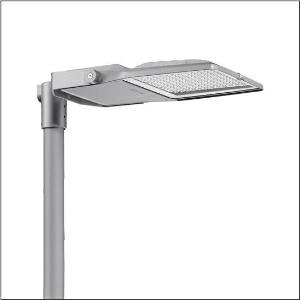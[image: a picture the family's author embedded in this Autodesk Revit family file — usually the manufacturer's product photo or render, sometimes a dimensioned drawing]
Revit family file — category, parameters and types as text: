
# Revit family: floodlight_fl_21_iq_midi___pl61_5xa7781e2c3a_352e
name_source: partatom
category: Lighting Fixtures
units: mm (PartAtom-declared; Revit-internal decimal feet)

## family parameters
Cut with Voids When Loaded = No
Host = Face
Light Source = No
Part Type = Normal
Room Calculation Point = No
Round Connector Dimension = Use Diameter
Shared = No

## types (1)
- --- (1 x LED, 26360 lm, 208.1 W, 3000K)
    Apparent Load = 208 VA
    CIE Flux Codes = 33 65 98 100 100
    Color Rendering = 70
    Color Temperature = 3000K
    Default Elevation = 1800 mm
    Description = Floodlight FL 21 iQ midi, floodlight, primary light control with lens, of PMMA, primary optical cover: protective disc, of toughened safety glass, transparent, light distribution: PL61, light emission: direct distribution, installation type: surface-mounted, LED, High Power LED, rated luminous flux: 26.360lm, luminous efficacy: 127lm/W, light colour: 730, colour temperature: 3000K, control gear: ECG iQ, control: optimised constant luminous flux control (CLO 2.0), Desk-Remote (wireless, voltage-free reading and setting of iQ features in the workshop via application-optimized NFC function/RFID function), Light-Fading, Smart-Wire, Night-Set, Lumen-Switch, Temp-Guard, Auto-Match, with terminal, 6-pole, mains connection: 220..240V, AC, 50/60Hz, start of lifetime: 208W, end of service life: 227W, reduction: 90W, luminaire housing, of diecast aluminium, powder-coated, Siteco® metallic grey (DB 702S), corrosivity category C5 mid according to DIN EN ISO 12944, sealing non-destructively replaceable, please order mast flange separately, mast bracket, of steel, galvanised, powder-coated, Siteco® metallic grey (DB 702S), protection rating (complete): IP66, insulation class (complete): insulation class II (safety insulation), certification: CE, protection symbol: D, impact resistance: IK08, permissible operating ambient temperature: -40..+40°C, permissible operating ambient temperature for outdoor applications: -40..+50°C, standard: DIN EN 12944, LABS conformity tested according to VDMA 24364:2018-05, packaging unit: 1 piece

Light Distribution: PL61
    Height = 76 mm
    Lamp = 1 x LED
    Lamp Light Flux = 26360 lm
    Lamp Power = 208.1 W
    Lamp count = 1
    Length = 657 mm
    Luminous efficacy = 127 lm/W
    Manufacturer = Siteco
    ModVariant = No
    Model = 5XA7781E2C3A
    Number of Poles = 1
    OnlyDefault = Yes
    Power Factor = 1
    Product Name = Floodlight FL 21 iQ midi | PL61
    Product group = floodlight | pylon annexe
    ProductGroupID = 6200
    Protection Class = Protection class II
    Protection Degree = IP 66
    RLX_Detail_Level = 1
    RLX_Emergency_Light_Flux = 0 lm
    RLX_Emergency_Type = 0
    RLX_Emergency_Type_DB = No
    RlxData = <blob elided: 153649 chars, md5=3d2aee96>
    Socket = socket
    Standby Power = 0 W
    System Light Flux = 26360 lm
    System Power = 208 W
    Type Comments = factory setting: luminous flux: 100 % | dim-lin: 254 | 710 mA
    Type Image = l_1007123.jpg
    URL = http://relux.com
    VarID = @adj_057223
    Voltage = 0 V
    Weight = 0.00 kg
    Width = 442 mm

## geometry (parser evidence)
native form markers: Blend x4, Sweep x15
no freeform markers — native parametric forms only
